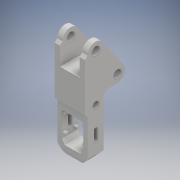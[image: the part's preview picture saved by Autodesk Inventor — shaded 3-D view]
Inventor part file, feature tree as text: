
AUTODESK INVENTOR PART (.ipt)
format: ipt  version: 2017 (Build 210142000, 142)  size: 386,560 bytes
history: native  units: mm
features: sketch x11, extrude x10, chamfer x7, other x3, plane x2, hole x1, mirror x1
ambient origin geometry x8: Origin, YZ Plane, XZ Plane, XY Plane, X Axis, Y Axis, Z Axis, Center Point
bodies: Body1 (feature_tree), Body2 (feature_tree)
feature tree (35):
  other  "Left"
  extrude  "Extrusion8"  Depth=9.0mm
  extrude  "Extrusion9"  Depth=24.3mm
  extrude  "Extrusion11"  Depth=18.0mm
  extrude  "Extrusion12"  Depth=18.0mm
  chamfer  "Chamfer5"  Distance=6.0mm
  extrude  "Extrusion13"  Depth=11.0mm TaperAngle=0.0deg
  hole  "Hole3"  [1 undecoded]
  extrude  "Extrusion14"  Depth=20.0mm
  chamfer  "Chamfer7"  Distance=3.0mm
  chamfer  "Chamfer8"  Distance=2.0mm Angle=45.0deg
  chamfer  "Chamfer9"  Distance=3.0mm
  plane  "Work Plane1"
  extrude  "Extrusion15"  Depth=24.0mm
  chamfer  "Chamfer10"  Distance=3.5mm
  extrude  "Extrusion16"  Depth=2.0mm TaperAngle=45.0deg
  chamfer  "Chamfer11"  Distance=4.5mm Angle=45.0deg
  plane  "Work Plane2"
  extrude  "Extrusion24"  Depth=3.5mm TaperAngle=45.0deg
  mirror  "Mirror2"
  extrude  "Extrusion26"  Depth=1.0mm
  chamfer  "Chamfer16"  Distance=9.0mm
  sketch  "Sketch8"  dims[d64=9.0mm d65=9.0mm]
  sketch  "Sketch9"  dims[d66=34.6mm d67=24.3mm]
  sketch  "Sketch11"  dims[d68=18.0mm d69=18.0mm]
  sketch  "Sketch12"  dims[d70=60.0mm d71=18.0mm d72=6.0mm d73=0.0mm]
  sketch  "Sketch13"  dims[d74=20.0mm d75=11.0mm d76=0.0mm]
  sketch  "Sketch14"  dims[d80=36.0mm d85=1.0mm d86=0.0mm]
  sketch  "Sketch15"  dims[d87=3.9mm d88=20.0mm d90=18.0mm d91=20.0mm d93=12.0mm]
  sketch  "Sketch16"  dims[d96=3.0mm]
  sketch  "Sketch17"  dims[d97=9.0mm d98=3.0mm d99=0.0mm d100=0.8mm d101=2.0mm d102=45.0deg]
  sketch  "Sketch25"  dims[d103=4.0mm]
  other  "Pattern of Left:1"
  other  "Right"
  sketch  "Sketch26"  dims[d104=18.0mm d105=3.0mm d106=0.0mm d107=24.0mm d108=3.3mm d109=6.0mm d110=7.0mm d111=9.0mm d112=90.0deg d113=8.0mm d114=20.594885mm d118=3.5mm d119=0.0mm d120=1.5mm d121=2.0mm d122=45.0deg d123=3.25mm d124=4.5mm d125=45.0deg d126=3.5mm d127=4.5mm d128=45.0deg d129=1.0mm d130=9.0mm d131=0.0mm d132=1.0mm d133=4.5mm d134=45.0deg d135=3.0mm d136=0.0mm d137=3.0mm d138=4.5mm d139=45.0deg d186=2.0mm d189=10.0mm d190=0.0mm d193=5.6mm d194=5.6mm d195=3.0mm d196=0.0mm d197=1.5mm d198=2.0mm d199=45.0deg]
note: 1 required parameter value undecoded (feature->parameter linkage not recoverable at this tier; creation-order binding heuristic only, values carry confidence <= 0.55)
